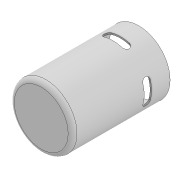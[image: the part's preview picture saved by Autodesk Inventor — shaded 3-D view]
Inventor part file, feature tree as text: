
AUTODESK INVENTOR PART (.ipt)
format: ipt  version: 2020 (Build 240168000, 168)  size: 199,680 bytes
history: native  units: mm
features: extrude x5, sketch x5, other x2, fillet x1, shell x1, pattern_circular x1
ambient origin geometry x8: Origin, YZ Plane, XZ Plane, XY Plane, X Axis, Y Axis, Z Axis, Center Point
bodies: Body1 (feature_tree)
feature tree (15):
  other  "솔리드1"
  extrude  "돌출1"  Depth=42.4mm
  extrude  "돌출2"  Depth=30.0mm TaperAngle=0.0deg
  extrude  "돌출3"  Depth=42.4mm
  fillet  "모깎기1"  Radius=30.0mm
  shell  "쉘1"  Thickness=42.4mm
  other  "작업 평면1"
  extrude  "돌출12"  Depth=6.0mm TaperAngle=0.0deg
  pattern_circular  "원형 패턴2"  [2 undecoded]
  extrude  "돌출13"  Depth=60.0mm
  sketch  "스케치1"
  sketch  "스케치2"
  sketch  "스케치3"
  sketch  "스케치12"
  sketch  "스케치13"
note: 2 required parameter values undecoded (feature->parameter linkage not recoverable at this tier; creation-order binding heuristic only, values carry confidence <= 0.55)
